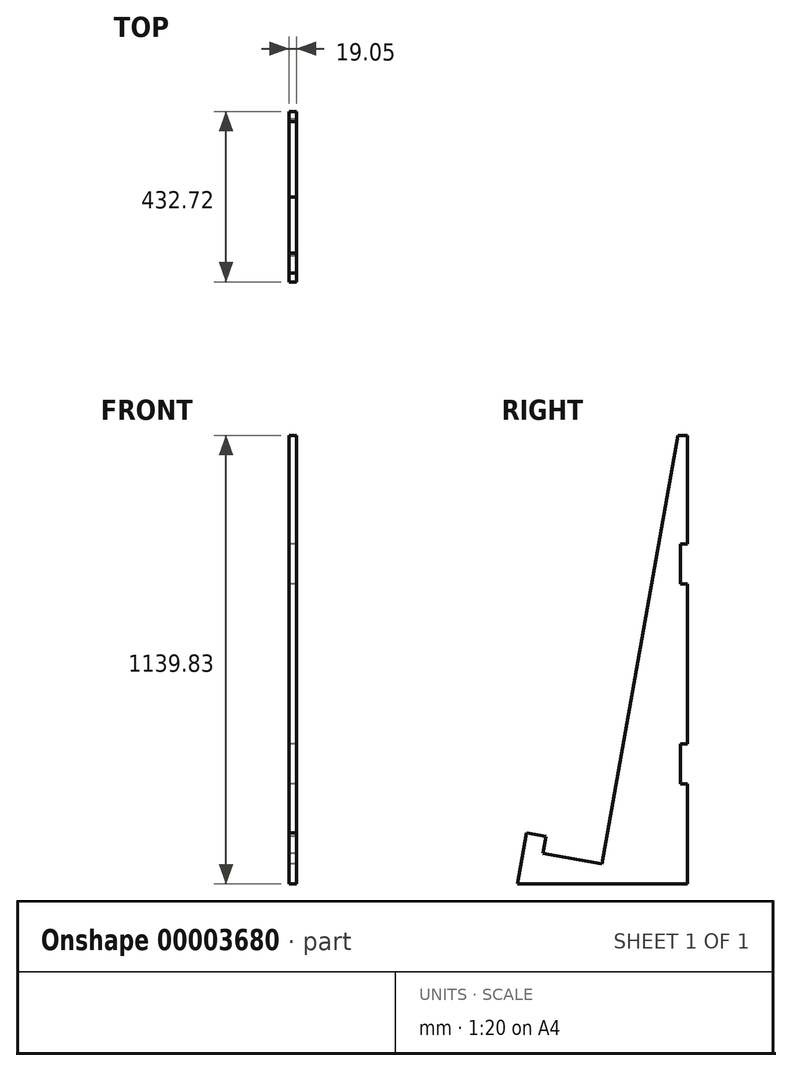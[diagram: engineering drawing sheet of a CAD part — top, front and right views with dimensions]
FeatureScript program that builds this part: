
annotation { "Feature Type Name" : "Feature", "Feature Type Description" : "" }
export const myFeature = defineFeature(function(context is Context, id is Id, definition is map)
    precondition{}
    {
        {
            var Q0;
            Q0=qCreatedBy(makeId("Right.planeOp"),FACE);
            var sketch = newSketch(context, id + "F0", { "sketchPlane" : qUnion([Q0])});
            skLineSegment(sketch, "E0", {"start": v(0, 0) * mm, "end": v(-432.72, 0) * mm});
            skLineSegment(sketch, "E1", {"start": v(-432.72, 0) * mm, "end": v(-409.82, 129.86) * mm});
            skLineSegment(sketch, "E2", {"start": v(-409.82, 129.86) * mm, "end": v(-359.8, 121.04) * mm});
            skLineSegment(sketch, "E3", {"start": v(-359.8, 121.04) * mm, "end": v(-367.5, 77.26) * mm});
            skLineSegment(sketch, "E4", {"start": v(-367.5, 77.26) * mm, "end": v(-217.42, 50.8) * mm});
            skLineSegment(sketch, "E5", {"start": v(-217.42, 50.8) * mm, "end": v(-25.4, 1139.83) * mm});
            skLineSegment(sketch, "E6", {"start": v(-25.4, 1139.83) * mm, "end": v(0, 1139.83) * mm});
            skLineSegment(sketch, "E7", {"start": v(0, 1139.83) * mm, "end": v(0, 863.6) * mm});
            skLineSegment(sketch, "E8", {"start": v(-217.42, -141.75) * mm, "end": v(-217.42, 464.23) * mm, "construction": true});
            skLineSegment(sketch, "E9", {"start": v(-217.42, 50.8) * mm, "end": v(-5.71, 1251.48) * mm, "construction": true});
            skLineSegment(sketch, "E10", {"start": v(0, 1250.47) * mm, "end": v(-5.71, 1251.48) * mm, "construction": true});
            skLineSegment(sketch, "E11", {"start": v(0, 1139.83) * mm, "end": v(0, 1334) * mm, "construction": true});
            skLineSegment(sketch, "E12", {"start": v(0, 0) * mm, "end": v(237.96, 0) * mm, "construction": true});
            skLineSegment(sketch, "E13", {"start": v(237.96, 0) * mm, "end": v(237.96, 1219.2) * mm, "construction": true});
            skLineSegment(sketch, "E14.bottom", {"start": v(0, 254) * mm, "end": v(-19.05, 254) * mm});
            skLineSegment(sketch, "E14.top", {"start": v(0, 355.6) * mm, "end": v(-19.05, 355.6) * mm});
            skLineSegment(sketch, "E14.right", {"start": v(-19.05, 254) * mm, "end": v(-19.05, 355.6) * mm});
            skLineSegment(sketch, "E15.bottom", {"start": v(0, 762) * mm, "end": v(-19.05, 762) * mm});
            skLineSegment(sketch, "E15.top", {"start": v(0, 863.6) * mm, "end": v(-19.05, 863.6) * mm});
            skLineSegment(sketch, "E15.right", {"start": v(-19.05, 762) * mm, "end": v(-19.05, 863.6) * mm});
            skLineSegment(sketch, "E16.trimOffspring", {"start": v(0, 762) * mm, "end": v(0, 355.6) * mm});
            skLineSegment(sketch, "E17.trimOffspring", {"start": v(0, 254) * mm, "end": v(0, 0) * mm});
            skSolve(sketch);
        }
        {
            var Q0;
            Q0=makeQuery(id+"F0.imprint","IMPRINT",FACE,{"disambiguationData":[TD([[makeQuery(id+"F0.imprint","IMPRINT",EDGE,{"derivedFrom":sQuery(id+"F0.wireOp",EDGE,"E0")}),-1.0]])]});
            extrude(context, id + "F1", {"entities" : qUnion([Q0]), "depth" : 19.05 * mm});
        }
    });
